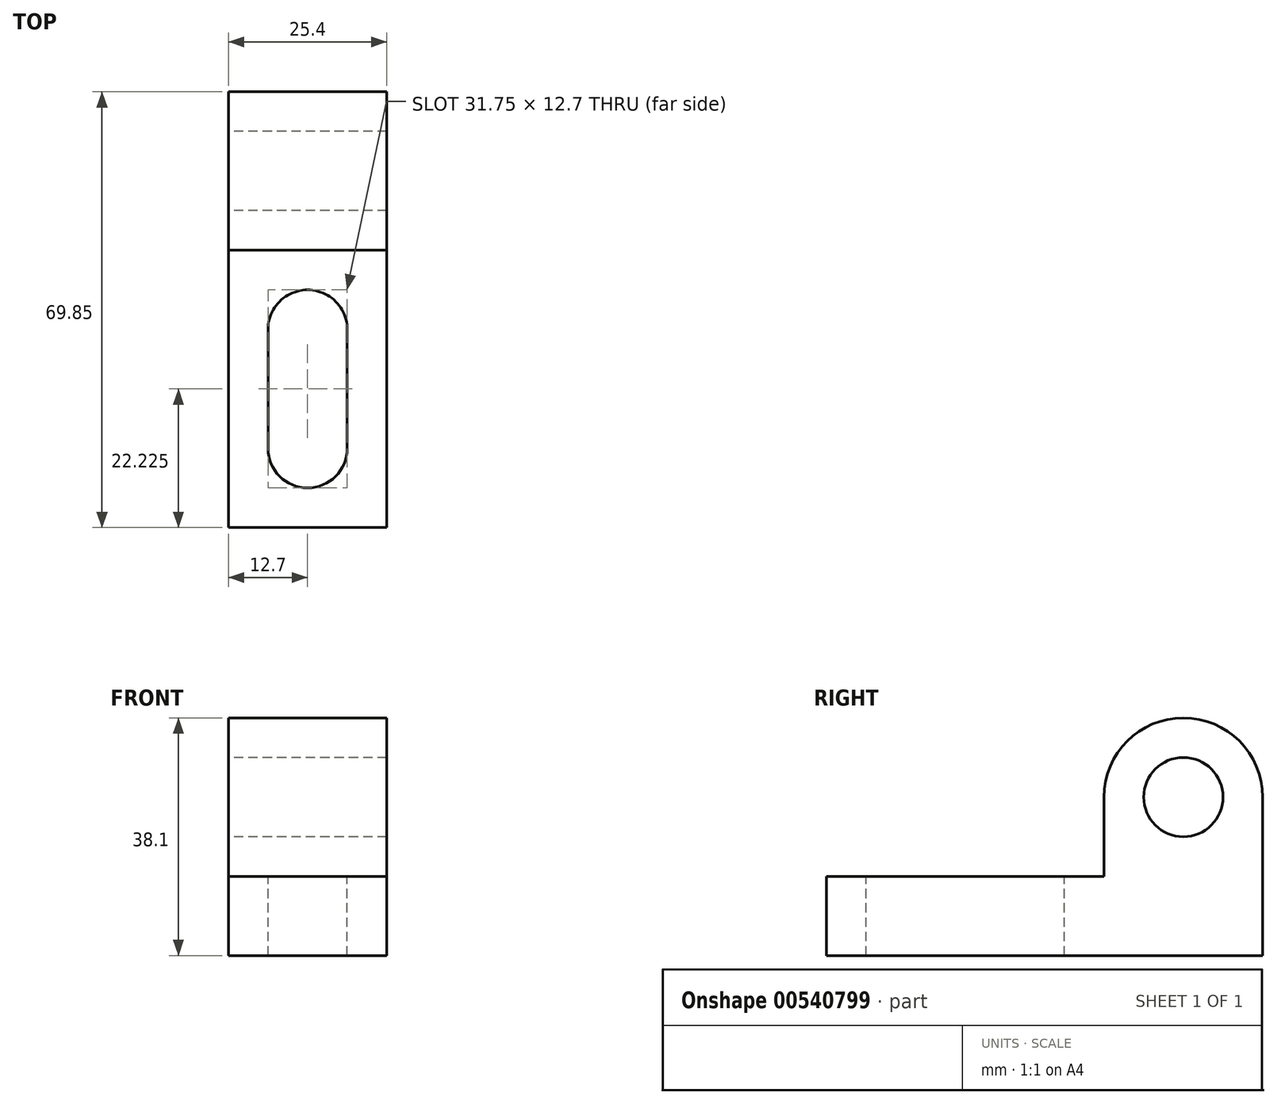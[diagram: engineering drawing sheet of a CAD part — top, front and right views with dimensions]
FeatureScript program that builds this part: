
annotation { "Feature Type Name" : "Feature", "Feature Type Description" : "" }
export const myFeature = defineFeature(function(context is Context, id is Id, definition is map)
    precondition{}
    {
        {
            var Q0;
            Q0=qCreatedBy(makeId("Top.planeOp"),FACE);
            var sketch = newSketch(context, id + "F0", { "sketchPlane" : qUnion([Q0])});
            skLineSegment(sketch, "E0", {"start": v(0, 0) * mm, "end": v(0, 69.85) * mm});
            skLineSegment(sketch, "E1", {"start": v(0, 69.85) * mm, "end": v(25.4, 69.85) * mm});
            skLineSegment(sketch, "E2", {"start": v(25.4, 69.85) * mm, "end": v(25.4, 0) * mm});
            skLineSegment(sketch, "E3", {"start": v(25.4, 0) * mm, "end": v(0, 0) * mm});
            skSolve(sketch);
        }
        {
            var Q0;
            Q0 = qSketchRegion(id + "F0", true);
            extrude(context, id + "F1", {"entities" : qUnion([Q0]), "depth" : 38.1 * mm, "offsetDistance" : 25.4 * mm});
        }
        {
            var Q0;
            Q0=makeQuery(id+"F1.opExtrude","SWEPT_FACE",FACE,{"disambiguationData":[OSD([sQuery(id+"F0.wireOp",EDGE,"E0")])]});
            var sketch = newSketch(context, id + "F2", { "sketchPlane" : qUnion([Q0])});
            skLineSegment(sketch, "E4", {"start": v(-44.45, 38.1) * mm, "end": v(-44.45, 12.7) * mm});
            skLineSegment(sketch, "E5", {"start": v(-44.45, 12.7) * mm, "end": v(0, 12.7) * mm});
            skLineSegment(sketch, "E6", {"start": v(0, 12.7) * mm, "end": v(0, 38.1) * mm});
            skLineSegment(sketch, "E7", {"start": v(0, 38.1) * mm, "end": v(-44.45, 38.1) * mm});
            skSolve(sketch);
        }
        {
            var Q0;
            Q0=makeQuery(id+"F2.imprint","IMPRINT",FACE,{"disambiguationData":[TD([[makeQuery(id+"F2.imprint","IMPRINT",EDGE,{"derivedFrom":sQuery(id+"F2.wireOp",EDGE,"E4")}),1.0]])]});
            extrude(context, id + "F3", {"entities" : qUnion([Q0]), "operationType" : NewBodyOperationType.REMOVE, "oppositeDirection" : true, "depth" : 25.4 * mm, "offsetDistance" : 25.4 * mm});
        }
        {
            var Q0;
            Q0=makeQuery(id+"F1.opExtrude","SWEPT_FACE",FACE,{"disambiguationData":[OSD([sQuery(id+"F0.wireOp",EDGE,"E0")])]});
            var sketch = newSketch(context, id + "F4", { "sketchPlane" : qUnion([Q0])});
            skLineSegment(sketch, "E8", {"start": v(-44.45, 12.7) * mm, "end": v(-44.45, 38.1) * mm});
            skLineSegment(sketch, "E9", {"start": v(-69.85, 38.1) * mm, "end": v(-69.85, 6.35) * mm});
            skArc(sketch, "E10", {"start": v(-44.45, 25.4) * mm, "mid": v(-57.15, 38.1) * mm, "end": v(-69.85, 25.4) * mm});
            skLineSegment(sketch, "E11", {"start": v(-69.85, 0) * mm, "end": v(0, 0) * mm});
            skSolve(sketch);
        }
        {
            var Q0;
            Q0 = qSketchRegion(id + "F4", true);
            var Q1;
            {var subQ0=sQuery(id+"F4.wireOp",EDGE,"E9");var subQ1=makeQuery(id+"F1.opExtrude","CAP_EDGE",EDGE,{"disambiguationData":[OSD([sQuery(id+"F0.wireOp",EDGE,"E0")])],"isStart":false});var subQ2=makeQuery(id+"F4.imprint","INTERSECT",VERTEX,{"derivedFrom":[subQ1,subQ0]});Q1=makeQuery(id+"F4.imprint","IMPRINT",FACE,{"disambiguationData":[TD([[makeQuery(id+"F4.imprint","IMPRINT",EDGE,{"disambiguationData":[TD([[subQ2,-1.0]])],"derivedFrom":subQ0}),1.0]])]});}
            var Q2;
            {var subQ0=sQuery(id+"F4.wireOp",EDGE,"E8");var subQ1=makeQuery(id+"F1.opExtrude","CAP_EDGE",EDGE,{"disambiguationData":[OSD([sQuery(id+"F0.wireOp",EDGE,"E0")])],"isStart":false});var subQ2=makeQuery(id+"F4.imprint","INTERSECT",VERTEX,{"derivedFrom":[subQ1,subQ0]});Q2=makeQuery(id+"F4.imprint","IMPRINT",FACE,{"disambiguationData":[TD([[makeQuery(id+"F4.imprint","IMPRINT",EDGE,{"disambiguationData":[TD([[subQ2,-1.0]])],"derivedFrom":subQ0}),-1.0]])]});}
            extrude(context, id + "F5", {"entities" : qUnion([Q0, Q1, Q2]), "operationType" : NewBodyOperationType.REMOVE, "oppositeDirection" : true, "depth" : 25.4 * mm, "offsetDistance" : 25.4 * mm});
        }
        {
            var Q0;
            Q0=makeQuery(id+"F1.opExtrude","SWEPT_FACE",FACE,{"disambiguationData":[OSD([sQuery(id+"F0.wireOp",EDGE,"E0")])]});
            var sketch = newSketch(context, id + "F6", { "sketchPlane" : qUnion([Q0])});
            skEllipse(sketch, "E12", {"center": v(-57.15, 25.4) * mm, "majorRadius": 6.35 * mm, "minorRadius": 6.35 * mm, "majorAxis": v(1, 0)});
            skSolve(sketch);
        }
        {
            var Q0;
            Q0=makeQuery(id+"F6.imprint","IMPRINT",FACE,{"disambiguationData":[TD([[makeQuery(id+"F6.imprint","IMPRINT",EDGE,{"derivedFrom":sQuery(id+"F6.wireOp",EDGE,"E12")}),1.0]])]});
            extrude(context, id + "F7", {"entities" : qUnion([Q0]), "operationType" : NewBodyOperationType.REMOVE, "oppositeDirection" : true, "depth" : 25.4 * mm, "offsetDistance" : 25.4 * mm});
        }
        {
            var Q0;
            Q0=makeQuery(id+"F3.boolean.opBoolean","COPY",FACE,{"derivedFrom":makeQuery(id+"F3.opExtrude","SWEPT_FACE",FACE,{"disambiguationData":[OSD([sQuery(id+"F2.wireOp",EDGE,"E5")])]})});
            var sketch = newSketch(context, id + "F8", { "sketchPlane" : qUnion([Q0])});
            skCircle(sketch, "E13", {"center": v(12.7, 31.75) * mm, "radius": 6.35 * mm});
            skCircle(sketch, "E14", {"center": v(12.7, 12.7) * mm, "radius": 6.35 * mm});
            skLineSegment(sketch, "E15", {"start": v(6.35, 31.74) * mm, "end": v(19.05, 31.74) * mm});
            skLineSegment(sketch, "E16", {"start": v(19.05, 31.74) * mm, "end": v(19.05, 12.69) * mm});
            skLineSegment(sketch, "E17", {"start": v(6.35, 31.74) * mm, "end": v(6.35, 12.69) * mm});
            skLineSegment(sketch, "E18", {"start": v(6.35, 12.69) * mm, "end": v(19.05, 12.69) * mm});
            skSolve(sketch);
        }
        {
            var Q0;
            {var subQ0=sQuery(id+"F8.wireOp",EDGE,"E18");Q0=makeQuery(id+"F8.imprint","IMPRINT",FACE,{"disambiguationData":[TD([[makeQuery(id+"F8.imprint","IMPRINT",EDGE,{"derivedFrom":subQ0}),-1.0]])]});}
            var Q1;
            {var subQ3=sQuery(id+"F8.wireOp",EDGE,"E18");Q1=makeQuery(id+"F8.imprint","IMPRINT",FACE,{"disambiguationData":[TD([[makeQuery(id+"F8.imprint","IMPRINT",EDGE,{"derivedFrom":subQ3}),1.0]])]});}
            var Q2;
            {var subQ3=sQuery(id+"F8.wireOp",EDGE,"E16");Q2=makeQuery(id+"F8.imprint","IMPRINT",FACE,{"disambiguationData":[TD([[makeQuery(id+"F8.imprint","IMPRINT",EDGE,{"derivedFrom":subQ3}),-1.0]])]});}
            var Q3;
            {var subQ0=sQuery(id+"F8.wireOp",EDGE,"E15");Q3=makeQuery(id+"F8.imprint","IMPRINT",FACE,{"disambiguationData":[TD([[makeQuery(id+"F8.imprint","IMPRINT",EDGE,{"derivedFrom":subQ0}),-1.0]])]});}
            var Q4;
            {var subQ0=sQuery(id+"F8.wireOp",EDGE,"E15");Q4=makeQuery(id+"F8.imprint","IMPRINT",FACE,{"disambiguationData":[TD([[makeQuery(id+"F8.imprint","IMPRINT",EDGE,{"derivedFrom":subQ0}),1.0]])]});}
            extrude(context, id + "F9", {"entities" : qUnion([Q0, Q1, Q2, Q3, Q4]), "operationType" : NewBodyOperationType.REMOVE, "oppositeDirection" : true, "depth" : 25.4 * mm, "offsetDistance" : 25.4 * mm});
        }
    });
